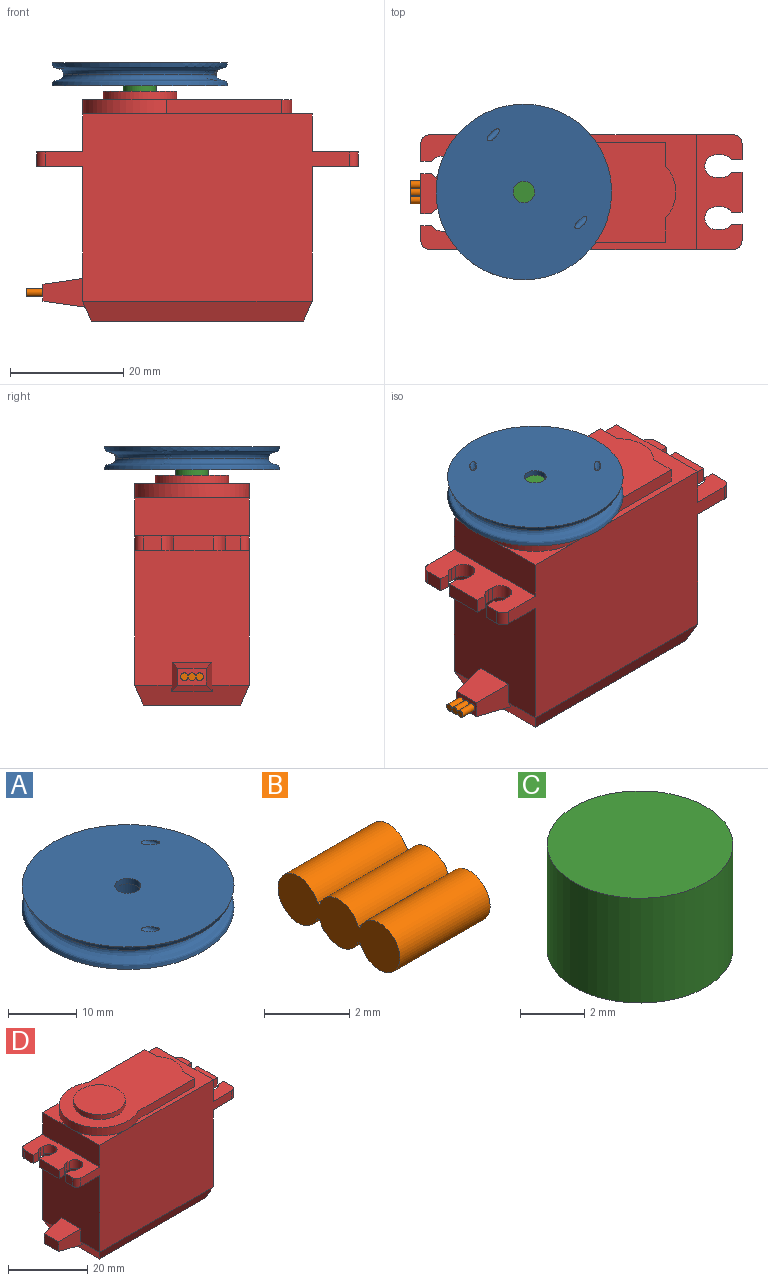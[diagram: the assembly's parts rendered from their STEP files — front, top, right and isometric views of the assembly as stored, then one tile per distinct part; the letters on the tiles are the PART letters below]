
ASSEMBLY  parts=4 mates=4
PART A: 9 faces, bbox 31x31x5.1 mm
  f0: revolved ~30.86x30.86mm, area 577.6mm2, adj f1,f6,f7,f8
  f1: revolved ~30.86x30.86mm, area 498.9mm2, adj f0,f2,f7,f8
  f2: plane 31x31mm, normal (0,0,1), area 738.2mm2, adj f1,f3,f7,f8
  f3: cylinder r=1.9mm len=3.8mm, axis (0,0,-1), area 11.9mm2, adj f2,f4
  f4: plane 5.8x5.8mm, normal (0,0,-1), area 15.1mm2, adj f3,f5
  f5: cylinder r=2.9mm len=5.8mm, axis (0,0,-1), area 54.7mm2, adj f4,f6
  f6: plane 31x31mm, normal (0,0,-1), area 728.3mm2, adj f0,f5
  f7: bspline ~5.54x5.54mm, area 19.3mm2, adj f0,f1,f2
  f8: bspline ~5.52x5.52mm, area 19.3mm2, adj f0,f1,f2
PART B: 10 faces, bbox 3x4.1x1.4 mm
  f0: plane 4.05x1.35mm, normal (-1,0,0), area 4.3mm2, adj f1,f2,f3,f4,f5,f6,f7,f8
  f1: plane 3x0.08mm, normal (0,0,1), area 0.2mm2, adj f0,f2,f8,f9
  f2: cylinder r=0.68mm len=3mm, axis (-1,0,0), area 5mm2, adj f0,f1,f3,f9
  f3: plane 3x0.08mm, normal (0,0,1), area 0.2mm2, adj f0,f2,f4,f9
  f4: cylinder r=0.68mm len=3mm, axis (-1,0,0), area 11.4mm2, adj f0,f3,f5,f9
  f5: plane 3x0.08mm, normal (0,0,-1), area 0.2mm2, adj f0,f4,f6,f9
  f6: cylinder r=0.68mm len=3mm, axis (-1,0,0), area 5mm2, adj f0,f5,f7,f9
  f7: plane 3x0.08mm, normal (0,0,-1), area 0.2mm2, adj f0,f6,f8,f9
  f8: cylinder r=0.68mm len=3mm, axis (-1,0,0), area 11.4mm2, adj f0,f1,f7,f9
  f9: plane 4.05x1.35mm, normal (1,0,0), area 4.3mm2, adj f1,f2,f3,f4,f5,f6,f7,f8
PART C: 3 faces, bbox 5.8x5.8x4 mm
  f0: plane 5.8x5.8mm, normal (0,0,1), area 26.4mm2, adj f1
  f1: cylinder r=2.9mm len=5.8mm, axis (0,0,-1), area 72.9mm2, adj f0,f2
  f2: plane 5.8x5.8mm, normal (0,0,-1), area 26.4mm2, adj f1
PART D: 70 faces, bbox 56.7x20.2x40.6 mm
  f0: plane 3.18x2.6mm, normal (-1,0,0), area 8.3mm2, adj f1,f2,f3,f4
  f1: plane 2.6x1.89mm, normal (0,-1,0), area 4.9mm2, adj f0,f3,f4,f55
  f2: cylinder r=1.5mm len=2.6mm, axis (0,0,-1), area 6.1mm2, adj f0,f3,f4,f20
  f3: plane 20.2x8.1mm, normal (0,0,1), area 122.2mm2, adj f0,f1,f2,f5,f6,f7,f8,f10
  f4: plane 20.2x8.1mm, normal (0,0,-1), area 122.2mm2, adj f0,f1,f2,f5,f6,f7,f8,f9
  f5: plane 2.6x1.89mm, normal (0,-1,0), area 4.9mm2, adj f3,f4,f49,f68
  f6: plane 2.6x1.89mm, normal (0,1,0), area 4.9mm2, adj f3,f4,f50,f69
  f7: plane 2.6x1.89mm, normal (0,1,0), area 4.9mm2, adj f3,f4,f56,f68
  f8: cylinder r=1.5mm len=2.6mm, axis (0,0,1), area 6.1mm2, adj f3,f4,f18,f69
  f9: plane 23.75x20.2mm, normal (-1,0,0), area 451.7mm2, adj f4,f18,f20,f58,f59,f61,f62
  f10: plane 20.2x6.7mm, normal (-1,0,0), area 135.3mm2, adj f3,f16,f18,f20,f21
  f11: plane 7.03x2.6mm, normal (1,0,0), area 18.3mm2, adj f13,f14,f39,f43
  f12: plane 2.92x2.6mm, normal (1,0,0), area 7.6mm2, adj f13,f14,f37,f67
  f13: plane 20.2x8.1mm, normal (0,0,-1), area 122.2mm2, adj f11,f12,f15,f18,f20,f32,f33,f34
  f14: plane 20.2x8.1mm, normal (0,0,1), area 122.2mm2, adj f11,f12,f18,f19,f20,f32,f33,f34
  f15: plane 23.75x20.2mm, normal (1,0,0), area 479.7mm2, adj f13,f18,f20,f65
  f16: plane 10.1x10.1mm, normal (0,0,1), area 21.9mm2, adj f10,f18,f27
  f17: plane 30.4x20.2mm, normal (0,0,1), area 151.9mm2, adj f18,f19,f20,f23,f24,f25,f26,f27
  f18: plane 53.7x33.05mm, normal (0,-1,0), area 1372.8mm2, adj f3,f4,f8,f9,f10,f13,f14,f15
  f19: plane 20.2x6.7mm, normal (1,0,0), area 135.3mm2, adj f14,f17,f18,f20
  f20: plane 53.7x33.05mm, normal (0,1,0), area 1372.8mm2, adj f2,f3,f4,f9,f10,f13,f14,f15
  f21: plane 10.1x10.1mm, normal (0,0,1), area 21.9mm2, adj f10,f20,f27
  f22: plane 37.5x17.2mm, normal (0,0,-1), area 645mm2, adj f62,f63,f64,f65
  f23: plane 4.4x2.5mm, normal (1,0,0), area 11mm2, adj f17,f24,f28,f29
  f24: cylinder r=6.4mm len=9mm, axis (0,0,-1), area 25mm2, adj f17,f23,f25,f29
  f25: plane 4.3x2.5mm, normal (1,0,0), area 10.8mm2, adj f17,f24,f26,f29
  f26: plane 20.04x2.5mm, normal (0,1,0), area 50.1mm2, adj f17,f25,f27,f29
  f27: cylinder r=10.1mm len=20.2mm, axis (0,0,-1), area 104.7mm2, adj f16,f17,f21,f26,f28,f29
  f28: plane 20.23x2.5mm, normal (0,-1,0), area 50.6mm2, adj f17,f23,f27,f29
  f29: plane 36.95x20.2mm, normal (0,0,1), area 489.7mm2, adj f23,f24,f25,f26,f27,f28,f30
  f30: cylinder r=6.5mm len=13mm, axis (0,0,-1), area 61.3mm2, adj f29,f31
  f31: plane 13x13mm, normal (0,0,1), area 132.7mm2, adj f30
  f32: plane 2.92x2.6mm, normal (1,0,0), area 7.6mm2, adj f13,f14,f44,f66
  f33: plane 2.6x1mm, normal (0,-1,0), area 2.6mm2, adj f13,f14,f34,f38
  f34: cylinder r=2mm len=4mm, axis (0,0,1), area 16.3mm2, adj f13,f14,f33,f35
  f35: plane 2.6x1mm, normal (0,1,0), area 2.6mm2, adj f13,f14,f34,f36
  f36: cylinder r=2mm len=2.6mm, axis (0,0,1), area 5.2mm2, adj f13,f14,f35,f37
  f37: plane 2.6x1.89mm, normal (0,1,0), area 4.9mm2, adj f12,f13,f14,f36
  f38: cylinder r=2mm len=2.6mm, axis (0,0,1), area 5.2mm2, adj f13,f14,f33,f39
  f39: plane 2.6x1.89mm, normal (0,-1,0), area 4.9mm2, adj f11,f13,f14,f38
  f40: cylinder r=2mm len=4mm, axis (0,0,1), area 16.3mm2, adj f13,f14,f41,f46
  f41: plane 2.6x1mm, normal (0,1,0), area 2.6mm2, adj f13,f14,f40,f42
  f42: cylinder r=2mm len=2.6mm, axis (0,0,1), area 5.2mm2, adj f13,f14,f41,f43
  f43: plane 2.6x1.89mm, normal (0,1,0), area 4.9mm2, adj f11,f13,f14,f42
  f44: plane 2.6x1.89mm, normal (0,-1,0), area 4.9mm2, adj f13,f14,f32,f45
  f45: cylinder r=2mm len=2.6mm, axis (0,0,1), area 5.2mm2, adj f13,f14,f44,f46
  f46: plane 2.6x1mm, normal (0,-1,0), area 2.6mm2, adj f13,f14,f40,f45
  f47: cylinder r=2mm len=4mm, axis (0,0,1), area 16.3mm2, adj f3,f4,f48,f51
  f48: plane 2.6x1mm, normal (0,-1,0), area 2.6mm2, adj f3,f4,f47,f49
  f49: cylinder r=2mm len=2.6mm, axis (0,0,1), area 5.2mm2, adj f3,f4,f5,f48
  f50: cylinder r=2mm len=2.6mm, axis (0,0,1), area 5.2mm2, adj f3,f4,f6,f51
  f51: plane 2.6x1mm, normal (0,1,0), area 2.6mm2, adj f3,f4,f47,f50
  f52: plane 2.6x1mm, normal (0,1,0), area 2.6mm2, adj f3,f4,f53,f56
  f53: cylinder r=2mm len=4mm, axis (0,0,1), area 16.3mm2, adj f3,f4,f52,f54
  f54: plane 2.6x1mm, normal (0,-1,0), area 2.6mm2, adj f3,f4,f53,f55
  f55: cylinder r=2mm len=2.6mm, axis (0,0,1), area 5.2mm2, adj f1,f3,f4,f54
  f56: cylinder r=2mm len=2.6mm, axis (0,0,1), area 5.2mm2, adj f3,f4,f7,f52
  f57: plane 5x3mm, normal (-1,0,0), area 15mm2, adj f58,f59,f60,f61
  f58: plane 7.46x5.07mm, normal (-0.14,-0.99,0), area 28.5mm2, adj f9,f57,f59,f60,f62
  f59: plane 7x7mm, normal (-0.14,0,0.99), area 42.4mm2, adj f9,f57,f58,f61
  f60: plane 7.46x7.13mm, normal (-0.14,0,-0.99), area 45.7mm2, adj f57,f58,f61,f62
  f61: plane 7.46x5.07mm, normal (-0.14,0.99,0), area 28.5mm2, adj f9,f57,f59,f60,f62
  f62: plane 20.2x3.5mm, normal (-0.92,0,-0.39), area 63mm2, adj f9,f22,f58,f60,f61,f63,f64
  f63: plane 40.5x3.5mm, normal (0,-0.92,-0.39), area 148.5mm2, adj f18,f22,f62,f65
  f64: plane 40.5x3.5mm, normal (0,0.92,-0.39), area 148.5mm2, adj f20,f22,f62,f65
  f65: plane 20.2x3.5mm, normal (0.92,0,-0.39), area 71.2mm2, adj f15,f22,f63,f64
  f66: cylinder r=1.5mm len=2.6mm, axis (0,0,-1), area 6.1mm2, adj f13,f14,f20,f32
  f67: cylinder r=1.5mm len=2.6mm, axis (0,0,1), area 6.1mm2, adj f12,f13,f14,f18
  f68: plane 7.03x2.6mm, normal (-1,0,0), area 18.3mm2, adj f3,f4,f5,f7
  f69: plane 2.65x2.6mm, normal (-1,0,0), area 6.9mm2, adj f3,f4,f6,f8
PLACE A rot(axis=(0,0,1),90deg) t=(6.63,22.76,39.89)mm
PLACE B t=(-3.47,12.56,-1.66)mm
PLACE C t=(-3.47,12.66,-1.66)mm
PLACE D t=(-3.47,12.66,-1.66)mm fixed
MATE planar C.f1 <-> A.f3  axis (0,0,1) through (6.63,22.76,42.89)mm
MATE fastened B.f2 <-> D.f57  axis (1,0,0) through (-10.47,22.76,3.34)mm
MATE fastened C.f1 <-> D.f27  axis (0,0,-1) through (6.63,22.76,38.89)mm
MATE slider A.f3 <-> C.f1  axis (0,0,-1) through (6.63,22.76,42.89)mm
